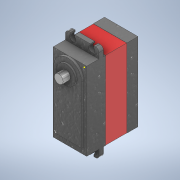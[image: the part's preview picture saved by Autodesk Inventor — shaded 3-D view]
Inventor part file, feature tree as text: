
AUTODESK INVENTOR PART (.ipt)
format: ipt  version: 2021 (Build 250183000, 183)  size: 227,328 bytes
history: native  units: mm
features: sketch x8, extrude x7, projected_geometry x2, plane x1, fillet x1
ambient origin geometry x8: Origin, YZ Plane, XZ Plane, XY Plane, X Axis, Y Axis, Z Axis, Center Point
bodies: Solid1 (feature_tree)
feature tree (19):
  extrude  "Extrusion1"  Depth=70.0mm
  extrude  "Extrusion2"  Depth=19.0mm TaperAngle=0.0deg
  extrude  "Extrusion3"  Depth=17.0mm
  extrude  "Extrusion4"  Depth=1.5mm
  extrude  "Extrusion5"  [1 undecoded]
  plane  "Work Plane1"
  extrude  "Extrusion6"  Depth=8.0mm
  fillet  "Fillet1"  Radius=5.5mm
  sketch  "Sketch7"  dims[d18=5.5mm d19=3.5mm d20=3.5mm d21=6.5mm]
  extrude  "Extrusion7"  Depth=3.5mm
  sketch  "Sketch1"  dims[d0=30.0mm d1=70.0mm]
  sketch  "Sketch2"  dims[d2=10.0mm d3=0.0mm d4=19.0mm d5=0.0mm]
  projected_geometry  "Projected Loop1"
  sketch  "Sketch3"  dims[d6=19.0mm d7=0.0mm d8=17.0mm]
  projected_geometry  "Projected Loop2"
  sketch  "Sketch4"  dims[d9=1.5mm d10=0.0mm d11=7.8mm]
  sketch  "Sketch5"  dims[d12=6.5mm d13=0.0mm d14=-17.0mm]
  sketch  "Sketch6"  dims[d15=30.0mm d16=8.0mm d17=5.5mm]
  sketch  "Sketch8"  dims[d22=6.5mm d23=4.0mm d24=0.0mm d25=3.0mm d26=12.5mm d27=2.0mm d28=0.0mm d29=0.1mm d30=0.1mm d31=0.1mm]
note: 1 required parameter value undecoded (feature->parameter linkage not recoverable at this tier; creation-order binding heuristic only, values carry confidence <= 0.55)
